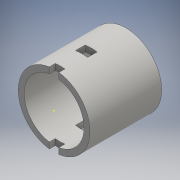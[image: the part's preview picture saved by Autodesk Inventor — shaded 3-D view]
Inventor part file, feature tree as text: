
AUTODESK INVENTOR PART (.ipt)
format: ipt  version: 2016 (Build 200138000, 138)  size: 125,952 bytes
history: native  units: mm
features: sketch x4, extrude x3, other x1
ambient origin geometry x8: Origin, YZ Plane, XZ Plane, XY Plane, X Axis, Y Axis, Z Axis, Center Point
bodies: Body1 (feature_tree)
feature tree (8):
  other  "ソリッド1"
  extrude  "押し出し1"  Depth=50.0mm
  extrude  "押し出し2"  Depth=60.0mm
  sketch  "スケッチ3"
  extrude  "押し出し3"  Depth=60.0mm TaperAngle=0.0deg
  sketch  "スケッチ1"
  sketch  "スケッチ2"
  sketch  "スケッチ4"
